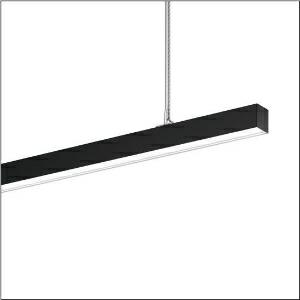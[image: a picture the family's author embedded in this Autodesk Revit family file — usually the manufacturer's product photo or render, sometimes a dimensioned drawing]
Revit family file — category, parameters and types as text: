
# Revit family: silica_r__21_51mx33tbt9b_b685
name_source: partatom
category: Lighting Fixtures
units: mm (PartAtom-declared; Revit-internal decimal feet)

## family parameters
Cut with Voids When Loaded = No
Host = Face
Light Source = No
Part Type = Normal
Room Calculation Point = No
Round Connector Dimension = Use Diameter
Shared = No

## types (1)
- --- (1 x LED, 7170 lm, 67.4 W, 6500K)
    Apparent Load = 67 VA
    CIE Flux Codes = 78 96 99 56 100
    Color Rendering = 80
    Color Temperature = 6500K
    Default Elevation = 1800 mm
    Description = Silica® 21, office luminaire, primary optical cover: prismatic diffuser, of PMMA, CAT 2 (L<= 3000cd/m²), light emission: direct/indirect distribution, primary light characteristic: symmetric, installation type: suspended mounting, LED, rated luminous flux: 7.170lm, luminous efficacy: 101lm/W, light colour: 8tw, colour temperature: 2700..6500K, control gear: DALI DT8, with terminal, 3+2-pole, max. 2.5mm², mains connection: 220..240V, AC, 50/60Hz, rated input power: 70.8W, luminaire housing, of aluminium, matt jet black (RAL 9005), length: 1.504mm, width: 53mm, height: 53mm, protection rating (complete): IP20, insulation class (complete): insulation class I (protective earthing), certification: CE, permissible operating ambient temperature: 0..+35°C, standard: EN 50419, packaging unit: 1 piece
    Height = 53 mm
    Lamp = 1 x LED
    Lamp Light Flux = 7170 lm
    Lamp Power = 67.4 W
    Lamp count = 1
    Length = 1504 mm
    Luminous efficacy = 106 lm/W
    Manufacturer = Siteco
    ModVariant = No
    Model = 51MX33TBT9B
    Mounting Place = Ceiling
    Mounting Type = Pendant
    Number of Poles = 1
    OnlyDefault = Yes
    Power Factor = 1
    Product Name = Silica® 21
    Product group = office luminaire | ceiling pendant
    ProductGroupID = 904
    Protection Class = Protection class I
    Protection Degree = IP 20
    RLX_Detail_Level = 1
    RLX_Emergency_Light_Flux = 0 lm
    RLX_Emergency_Type = 0
    RLX_Emergency_Type_DB = No
    RlxData = <blob elided: 22917 chars, md5=22ff0969>
    Socket = socket
    Standby Power = 0 W
    System Light Flux = 7170 lm
    System Power = 67 W
    Type Comments = individual setting
    Type Image = l_1335856.jpg
    URL = http://relux.com
    VarID = @adj_139758
    Voltage = 0 V
    Weight = 0.00 kg
    Width = 53 mm

## geometry (parser evidence)
native form markers: Blend x4, Sweep x13
no freeform markers — native parametric forms only
